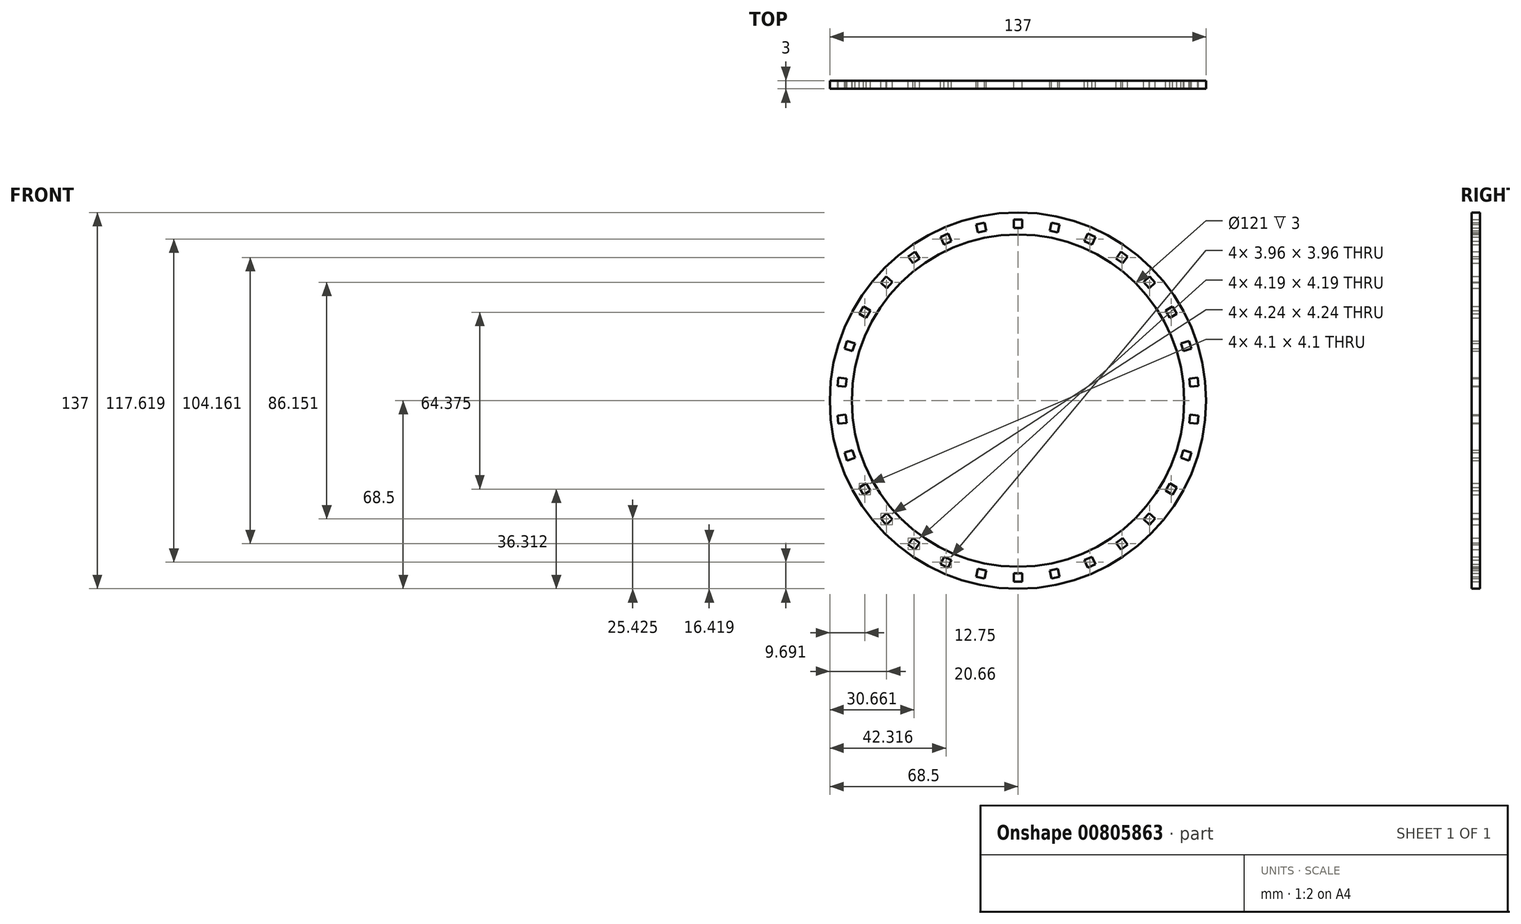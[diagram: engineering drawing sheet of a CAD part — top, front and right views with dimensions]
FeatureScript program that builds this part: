
annotation { "Feature Type Name" : "Feature", "Feature Type Description" : "" }
export const myFeature = defineFeature(function(context is Context, id is Id, definition is map)
    precondition{}
    {
        {
            var Q0;
            Q0=qCreatedBy(makeId("Front.planeOp"),FACE);
            var sketch = newSketch(context, id + "F0", { "sketchPlane" : qUnion([Q0])});
            skCircle(sketch, "E0", {"center": v(0, 0) * mm, "radius": 68.5 * mm});
            skCircle(sketch, "E1", {"center": v(0, 0) * mm, "radius": 60.5 * mm});
            skSolve(sketch);
        }
        {
            var Q0;
            Q0=makeQuery(id+"F0.imprint","IMPRINT",FACE,{"disambiguationData":[TD([[makeQuery(id+"F0.imprint","IMPRINT",EDGE,{"derivedFrom":sQuery(id+"F0.wireOp",EDGE,"E0")}),1.0]])]});
            extrude(context, id + "F1", {"entities" : qUnion([Q0]), "depth" : 3 * mm, "offsetDistance" : 25 * mm});
        }
        {
            var Q0;
            Q0=qCreatedBy(makeId("Front.planeOp"),FACE);
            var sketch = newSketch(context, id + "F2", { "sketchPlane" : qUnion([Q0])});
            skLineSegment(sketch, "E2.bottom", {"start": v(-1.5, 65.88) * mm, "end": v(1.5, 65.88) * mm});
            skLineSegment(sketch, "E2.top", {"start": v(-1.5, 62.88) * mm, "end": v(1.5, 62.88) * mm});
            skLineSegment(sketch, "E2.left", {"start": v(-1.5, 65.88) * mm, "end": v(-1.5, 62.88) * mm});
            skLineSegment(sketch, "E2.right", {"start": v(1.5, 65.88) * mm, "end": v(1.5, 62.88) * mm});
            skLineSegment(sketch, "E3.1.0", {"start": v(-15.16, 64.12) * mm, "end": v(-12.23, 64.75) * mm});
            skLineSegment(sketch, "E3.1.1", {"start": v(-12.23, 64.75) * mm, "end": v(-11.6, 61.81) * mm});
            skLineSegment(sketch, "E3.1.2", {"start": v(-14.54, 61.19) * mm, "end": v(-11.6, 61.81) * mm});
            skLineSegment(sketch, "E3.1.3", {"start": v(-15.16, 64.12) * mm, "end": v(-14.54, 61.19) * mm});
            skLineSegment(sketch, "E3.2.0", {"start": v(-28.16, 59.57) * mm, "end": v(-25.42, 60.79) * mm});
            skLineSegment(sketch, "E3.2.1", {"start": v(-25.42, 60.79) * mm, "end": v(-24.2, 58.05) * mm});
            skLineSegment(sketch, "E3.2.2", {"start": v(-26.94, 56.83) * mm, "end": v(-24.2, 58.05) * mm});
            skLineSegment(sketch, "E3.2.3", {"start": v(-28.16, 59.57) * mm, "end": v(-26.94, 56.83) * mm});
            skPoint(sketch, "E3.center", {"position": v(0, 0) * mm});
            skLineSegment(sketch, "E4.3.3.0", {"start": v(-37.5, 54.18) * mm, "end": v(-35.74, 51.75) * mm});
            skLineSegment(sketch, "E4.6.3.0", {"start": v(-38.17, 49.99) * mm, "end": v(-35.74, 51.75) * mm});
            skLineSegment(sketch, "E4.7.3.0", {"start": v(-39.93, 52.41) * mm, "end": v(-37.5, 54.18) * mm});
            skLineSegment(sketch, "E4.9.3.0", {"start": v(-39.93, 52.41) * mm, "end": v(-38.17, 49.99) * mm});
            skLineSegment(sketch, "E4.3.4.0", {"start": v(-47.95, 45.2) * mm, "end": v(-45.72, 43.19) * mm});
            skLineSegment(sketch, "E4.6.4.0", {"start": v(-47.73, 40.96) * mm, "end": v(-45.72, 43.19) * mm});
            skLineSegment(sketch, "E4.7.4.0", {"start": v(-49.96, 42.96) * mm, "end": v(-47.95, 45.2) * mm});
            skLineSegment(sketch, "E4.9.4.0", {"start": v(-49.96, 42.96) * mm, "end": v(-47.73, 40.96) * mm});
            skLineSegment(sketch, "E4.3.5.0", {"start": v(-56.3, 34.24) * mm, "end": v(-53.7, 32.74) * mm});
            skLineSegment(sketch, "E4.6.5.0", {"start": v(-55.2, 30.14) * mm, "end": v(-53.7, 32.74) * mm});
            skLineSegment(sketch, "E4.7.5.0", {"start": v(-57.8, 31.64) * mm, "end": v(-56.3, 34.24) * mm});
            skLineSegment(sketch, "E4.9.5.0", {"start": v(-57.8, 31.64) * mm, "end": v(-55.2, 30.14) * mm});
            skLineSegment(sketch, "E4.3.6.0", {"start": v(-62.19, 21.78) * mm, "end": v(-59.33, 20.86) * mm});
            skLineSegment(sketch, "E4.6.6.0", {"start": v(-60.26, 18) * mm, "end": v(-59.33, 20.86) * mm});
            skLineSegment(sketch, "E4.7.6.0", {"start": v(-63.11, 18.93) * mm, "end": v(-62.19, 21.78) * mm});
            skLineSegment(sketch, "E4.9.6.0", {"start": v(-63.11, 18.93) * mm, "end": v(-60.26, 18) * mm});
            skLineSegment(sketch, "E4.3.7.0", {"start": v(-65.36, 8.38) * mm, "end": v(-62.37, 8.06) * mm});
            skLineSegment(sketch, "E4.6.7.0", {"start": v(-62.69, 5.08) * mm, "end": v(-62.37, 8.06) * mm});
            skLineSegment(sketch, "E4.7.7.0", {"start": v(-65.67, 5.4) * mm, "end": v(-65.36, 8.38) * mm});
            skLineSegment(sketch, "E4.9.7.0", {"start": v(-65.67, 5.4) * mm, "end": v(-62.69, 5.08) * mm});
            skLineSegment(sketch, "E4.3.8.0", {"start": v(-65.67, -5.4) * mm, "end": v(-62.69, -5.08) * mm});
            skLineSegment(sketch, "E4.6.8.0", {"start": v(-62.37, -8.06) * mm, "end": v(-62.69, -5.08) * mm});
            skLineSegment(sketch, "E4.7.8.0", {"start": v(-65.36, -8.38) * mm, "end": v(-65.67, -5.4) * mm});
            skLineSegment(sketch, "E4.9.8.0", {"start": v(-65.36, -8.38) * mm, "end": v(-62.37, -8.06) * mm});
            skLineSegment(sketch, "E4.3.9.0", {"start": v(-63.11, -18.93) * mm, "end": v(-60.26, -18) * mm});
            skLineSegment(sketch, "E4.6.9.0", {"start": v(-59.33, -20.86) * mm, "end": v(-60.26, -18) * mm});
            skLineSegment(sketch, "E4.7.9.0", {"start": v(-62.19, -21.78) * mm, "end": v(-63.11, -18.93) * mm});
            skLineSegment(sketch, "E4.9.9.0", {"start": v(-62.19, -21.78) * mm, "end": v(-59.33, -20.86) * mm});
            skLineSegment(sketch, "E4.3.10.0", {"start": v(-57.8, -31.64) * mm, "end": v(-55.2, -30.14) * mm});
            skLineSegment(sketch, "E4.6.10.0", {"start": v(-53.7, -32.74) * mm, "end": v(-55.2, -30.14) * mm});
            skLineSegment(sketch, "E4.7.10.0", {"start": v(-56.3, -34.24) * mm, "end": v(-57.8, -31.64) * mm});
            skLineSegment(sketch, "E4.9.10.0", {"start": v(-56.3, -34.24) * mm, "end": v(-53.7, -32.74) * mm});
            skLineSegment(sketch, "E4.3.11.0", {"start": v(-49.96, -42.96) * mm, "end": v(-47.73, -40.96) * mm});
            skLineSegment(sketch, "E4.6.11.0", {"start": v(-45.72, -43.19) * mm, "end": v(-47.73, -40.96) * mm});
            skLineSegment(sketch, "E4.7.11.0", {"start": v(-47.95, -45.2) * mm, "end": v(-49.96, -42.96) * mm});
            skLineSegment(sketch, "E4.9.11.0", {"start": v(-47.95, -45.2) * mm, "end": v(-45.72, -43.19) * mm});
            skLineSegment(sketch, "E4.3.12.0", {"start": v(-39.93, -52.41) * mm, "end": v(-38.17, -49.99) * mm});
            skLineSegment(sketch, "E4.6.12.0", {"start": v(-35.74, -51.75) * mm, "end": v(-38.17, -49.99) * mm});
            skLineSegment(sketch, "E4.7.12.0", {"start": v(-37.5, -54.18) * mm, "end": v(-39.93, -52.41) * mm});
            skLineSegment(sketch, "E4.9.12.0", {"start": v(-37.5, -54.18) * mm, "end": v(-35.74, -51.75) * mm});
            skLineSegment(sketch, "E4.3.13.0", {"start": v(-28.16, -59.57) * mm, "end": v(-26.94, -56.83) * mm});
            skLineSegment(sketch, "E4.6.13.0", {"start": v(-24.2, -58.05) * mm, "end": v(-26.94, -56.83) * mm});
            skLineSegment(sketch, "E4.7.13.0", {"start": v(-25.42, -60.79) * mm, "end": v(-28.16, -59.57) * mm});
            skLineSegment(sketch, "E4.9.13.0", {"start": v(-25.42, -60.79) * mm, "end": v(-24.2, -58.05) * mm});
            skLineSegment(sketch, "E4.3.14.0", {"start": v(-15.16, -64.12) * mm, "end": v(-14.54, -61.19) * mm});
            skLineSegment(sketch, "E4.6.14.0", {"start": v(-11.6, -61.81) * mm, "end": v(-14.54, -61.19) * mm});
            skLineSegment(sketch, "E4.7.14.0", {"start": v(-12.23, -64.75) * mm, "end": v(-15.16, -64.12) * mm});
            skLineSegment(sketch, "E4.9.14.0", {"start": v(-12.23, -64.75) * mm, "end": v(-11.6, -61.81) * mm});
            skLineSegment(sketch, "E4.3.15.0", {"start": v(-1.5, -65.88) * mm, "end": v(-1.5, -62.88) * mm});
            skLineSegment(sketch, "E4.6.15.0", {"start": v(1.5, -62.88) * mm, "end": v(-1.5, -62.88) * mm});
            skLineSegment(sketch, "E4.7.15.0", {"start": v(1.5, -65.88) * mm, "end": v(-1.5, -65.88) * mm});
            skLineSegment(sketch, "E4.9.15.0", {"start": v(1.5, -65.88) * mm, "end": v(1.5, -62.88) * mm});
            skLineSegment(sketch, "E4.3.16.0", {"start": v(12.23, -64.75) * mm, "end": v(11.6, -61.81) * mm});
            skLineSegment(sketch, "E4.6.16.0", {"start": v(14.54, -61.19) * mm, "end": v(11.6, -61.81) * mm});
            skLineSegment(sketch, "E4.7.16.0", {"start": v(15.16, -64.12) * mm, "end": v(12.23, -64.75) * mm});
            skLineSegment(sketch, "E4.9.16.0", {"start": v(15.16, -64.12) * mm, "end": v(14.54, -61.19) * mm});
            skLineSegment(sketch, "E4.3.17.0", {"start": v(25.42, -60.79) * mm, "end": v(24.2, -58.05) * mm});
            skLineSegment(sketch, "E4.6.17.0", {"start": v(26.94, -56.83) * mm, "end": v(24.2, -58.05) * mm});
            skLineSegment(sketch, "E4.7.17.0", {"start": v(28.16, -59.57) * mm, "end": v(25.42, -60.79) * mm});
            skLineSegment(sketch, "E4.9.17.0", {"start": v(28.16, -59.57) * mm, "end": v(26.94, -56.83) * mm});
            skLineSegment(sketch, "E4.3.18.0", {"start": v(37.5, -54.18) * mm, "end": v(35.74, -51.75) * mm});
            skLineSegment(sketch, "E4.6.18.0", {"start": v(38.17, -49.99) * mm, "end": v(35.74, -51.75) * mm});
            skLineSegment(sketch, "E4.7.18.0", {"start": v(39.93, -52.41) * mm, "end": v(37.5, -54.18) * mm});
            skLineSegment(sketch, "E4.9.18.0", {"start": v(39.93, -52.41) * mm, "end": v(38.17, -49.99) * mm});
            skLineSegment(sketch, "E4.3.19.0", {"start": v(47.95, -45.2) * mm, "end": v(45.72, -43.19) * mm});
            skLineSegment(sketch, "E4.6.19.0", {"start": v(47.73, -40.96) * mm, "end": v(45.72, -43.19) * mm});
            skLineSegment(sketch, "E4.7.19.0", {"start": v(49.96, -42.96) * mm, "end": v(47.95, -45.2) * mm});
            skLineSegment(sketch, "E4.9.19.0", {"start": v(49.96, -42.96) * mm, "end": v(47.73, -40.96) * mm});
            skLineSegment(sketch, "E4.3.20.0", {"start": v(56.3, -34.24) * mm, "end": v(53.7, -32.74) * mm});
            skLineSegment(sketch, "E4.6.20.0", {"start": v(55.2, -30.14) * mm, "end": v(53.7, -32.74) * mm});
            skLineSegment(sketch, "E4.7.20.0", {"start": v(57.8, -31.64) * mm, "end": v(56.3, -34.24) * mm});
            skLineSegment(sketch, "E4.9.20.0", {"start": v(57.8, -31.64) * mm, "end": v(55.2, -30.14) * mm});
            skLineSegment(sketch, "E4.3.21.0", {"start": v(62.19, -21.78) * mm, "end": v(59.33, -20.86) * mm});
            skLineSegment(sketch, "E4.6.21.0", {"start": v(60.26, -18) * mm, "end": v(59.33, -20.86) * mm});
            skLineSegment(sketch, "E4.7.21.0", {"start": v(63.11, -18.93) * mm, "end": v(62.19, -21.78) * mm});
            skLineSegment(sketch, "E4.9.21.0", {"start": v(63.11, -18.93) * mm, "end": v(60.26, -18) * mm});
            skLineSegment(sketch, "E4.3.22.0", {"start": v(65.36, -8.38) * mm, "end": v(62.37, -8.06) * mm});
            skLineSegment(sketch, "E4.6.22.0", {"start": v(62.69, -5.08) * mm, "end": v(62.37, -8.06) * mm});
            skLineSegment(sketch, "E4.7.22.0", {"start": v(65.67, -5.4) * mm, "end": v(65.36, -8.38) * mm});
            skLineSegment(sketch, "E4.9.22.0", {"start": v(65.67, -5.4) * mm, "end": v(62.69, -5.08) * mm});
            skLineSegment(sketch, "E4.3.23.0", {"start": v(65.67, 5.4) * mm, "end": v(62.69, 5.08) * mm});
            skLineSegment(sketch, "E4.6.23.0", {"start": v(62.37, 8.06) * mm, "end": v(62.69, 5.08) * mm});
            skLineSegment(sketch, "E4.7.23.0", {"start": v(65.36, 8.38) * mm, "end": v(65.67, 5.4) * mm});
            skLineSegment(sketch, "E4.9.23.0", {"start": v(65.36, 8.38) * mm, "end": v(62.37, 8.06) * mm});
            skLineSegment(sketch, "E4.3.24.0", {"start": v(63.11, 18.93) * mm, "end": v(60.26, 18) * mm});
            skLineSegment(sketch, "E4.6.24.0", {"start": v(59.33, 20.86) * mm, "end": v(60.26, 18) * mm});
            skLineSegment(sketch, "E4.7.24.0", {"start": v(62.19, 21.78) * mm, "end": v(63.11, 18.93) * mm});
            skLineSegment(sketch, "E4.9.24.0", {"start": v(62.19, 21.78) * mm, "end": v(59.33, 20.86) * mm});
            skLineSegment(sketch, "E4.3.25.0", {"start": v(57.8, 31.64) * mm, "end": v(55.2, 30.14) * mm});
            skLineSegment(sketch, "E4.6.25.0", {"start": v(53.7, 32.74) * mm, "end": v(55.2, 30.14) * mm});
            skLineSegment(sketch, "E4.7.25.0", {"start": v(56.3, 34.24) * mm, "end": v(57.8, 31.64) * mm});
            skLineSegment(sketch, "E4.9.25.0", {"start": v(56.3, 34.24) * mm, "end": v(53.7, 32.74) * mm});
            skLineSegment(sketch, "E4.3.26.0", {"start": v(49.96, 42.96) * mm, "end": v(47.73, 40.96) * mm});
            skLineSegment(sketch, "E4.6.26.0", {"start": v(45.72, 43.19) * mm, "end": v(47.73, 40.96) * mm});
            skLineSegment(sketch, "E4.7.26.0", {"start": v(47.95, 45.2) * mm, "end": v(49.96, 42.96) * mm});
            skLineSegment(sketch, "E4.9.26.0", {"start": v(47.95, 45.2) * mm, "end": v(45.72, 43.19) * mm});
            skLineSegment(sketch, "E4.3.27.0", {"start": v(39.93, 52.41) * mm, "end": v(38.17, 49.99) * mm});
            skLineSegment(sketch, "E4.6.27.0", {"start": v(35.74, 51.75) * mm, "end": v(38.17, 49.99) * mm});
            skLineSegment(sketch, "E4.7.27.0", {"start": v(37.5, 54.18) * mm, "end": v(39.93, 52.41) * mm});
            skLineSegment(sketch, "E4.9.27.0", {"start": v(37.5, 54.18) * mm, "end": v(35.74, 51.75) * mm});
            skLineSegment(sketch, "E4.3.28.0", {"start": v(28.16, 59.57) * mm, "end": v(26.94, 56.83) * mm});
            skLineSegment(sketch, "E4.6.28.0", {"start": v(24.2, 58.05) * mm, "end": v(26.94, 56.83) * mm});
            skLineSegment(sketch, "E4.7.28.0", {"start": v(25.42, 60.79) * mm, "end": v(28.16, 59.57) * mm});
            skLineSegment(sketch, "E4.9.28.0", {"start": v(25.42, 60.79) * mm, "end": v(24.2, 58.05) * mm});
            skLineSegment(sketch, "E4.3.29.0", {"start": v(15.16, 64.12) * mm, "end": v(14.54, 61.19) * mm});
            skLineSegment(sketch, "E4.6.29.0", {"start": v(11.6, 61.81) * mm, "end": v(14.54, 61.19) * mm});
            skLineSegment(sketch, "E4.7.29.0", {"start": v(12.23, 64.75) * mm, "end": v(15.16, 64.12) * mm});
            skLineSegment(sketch, "E4.9.29.0", {"start": v(12.23, 64.75) * mm, "end": v(11.6, 61.81) * mm});
            skSolve(sketch);
        }
        {
            var Q0;
            Q0=qSketchRegion(id+"F2",true);
            extrude(context, id + "F3", {"entities" : qUnion([Q0]), "operationType" : NewBodyOperationType.REMOVE, "depth" : 3 * mm, "offsetDistance" : 25 * mm});
        }
    });
